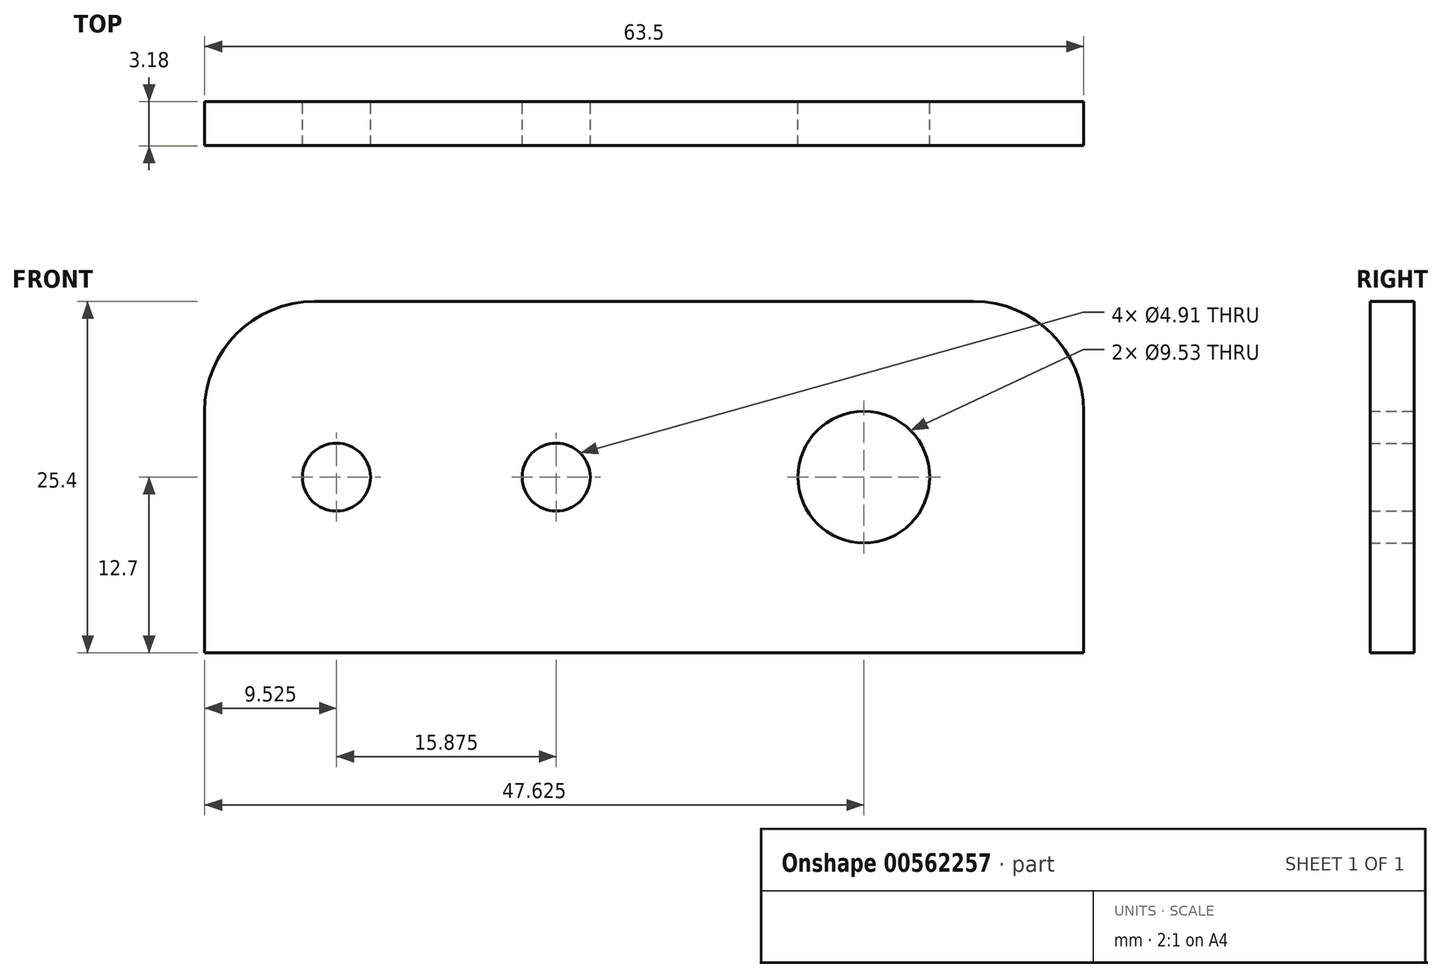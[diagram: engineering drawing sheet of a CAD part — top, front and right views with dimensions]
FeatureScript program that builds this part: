
annotation { "Feature Type Name" : "Feature", "Feature Type Description" : "" }
export const myFeature = defineFeature(function(context is Context, id is Id, definition is map)
    precondition{}
    {
        {
            var Q0;
            Q0=qCreatedBy(makeId("Front.planeOp"),FACE);
            var sketch = newSketch(context, id + "F0", { "sketchPlane" : qUnion([Q0])});
            skLineSegment(sketch, "E0.bottom", {"start": v(31.75, -12.7) * mm, "end": v(-31.75, -12.7) * mm});
            skLineSegment(sketch, "E0.top", {"start": v(23.81, 12.7) * mm, "end": v(-23.81, 12.7) * mm});
            skLineSegment(sketch, "E0.left", {"start": v(31.75, -12.7) * mm, "end": v(31.75, 4.76) * mm});
            skLineSegment(sketch, "E0.right", {"start": v(-31.75, -12.7) * mm, "end": v(-31.75, 4.76) * mm});
            skPoint(sketch, "E0.middle", {"position": v(0, 0) * mm});
            skPoint(sketch, "E1.visualSharp", {"position": v(-31.75, 12.7) * mm});
            skArc(sketch, "E1.filletArc", {"start": v(-23.81, 12.7) * mm, "mid": v(-29.43, 10.38) * mm, "end": v(-31.75, 4.76) * mm});
            skPoint(sketch, "E2.visualSharp", {"position": v(31.75, 12.7) * mm});
            skArc(sketch, "E2.filletArc", {"start": v(31.75, 4.76) * mm, "mid": v(29.43, 10.38) * mm, "end": v(23.81, 12.7) * mm});
            skCircle(sketch, "E3", {"center": v(-22.23, 0) * mm, "radius": 2.46 * mm});
            skCircle(sketch, "E4", {"center": v(-6.35, 0) * mm, "radius": 2.46 * mm});
            skCircle(sketch, "E5", {"center": v(15.88, 0) * mm, "radius": 4.76 * mm});
            skSolve(sketch);
        }
        {
            var Q0;
            Q0 = qSketchRegion(id + "F0", true);
            extrude(context, id + "F1", {"entities" : qUnion([Q0]), "depth" : 3.17 * mm, "offsetDistance" : 25.4 * mm});
        }
    });
